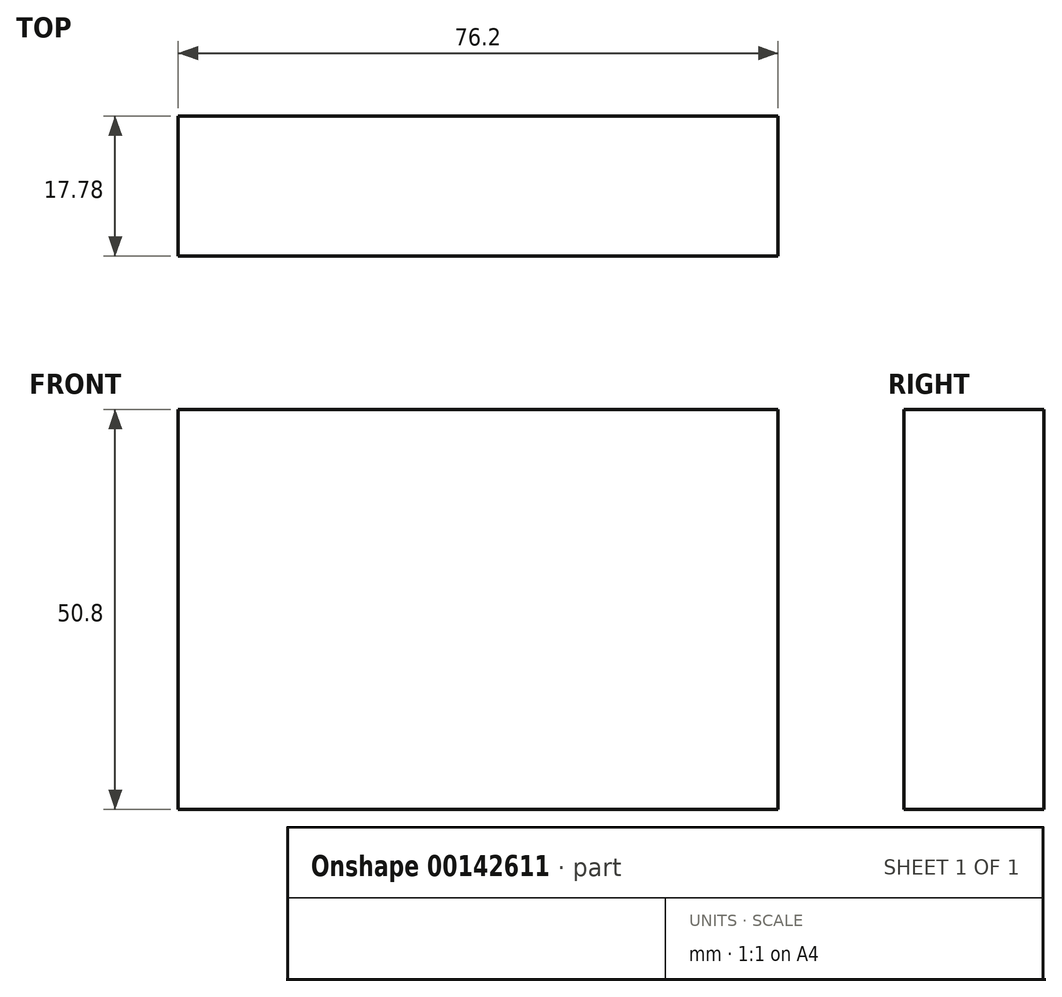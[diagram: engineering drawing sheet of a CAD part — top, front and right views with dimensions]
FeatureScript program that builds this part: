
annotation { "Feature Type Name" : "Feature", "Feature Type Description" : "" }
export const myFeature = defineFeature(function(context is Context, id is Id, definition is map)
    precondition{}
    {
        {
            var Q0;
            Q0=qCreatedBy(makeId("Top.planeOp"),FACE);
            var sketch = newSketch(context, id + "F0", { "sketchPlane" : qUnion([Q0])});
            skLineSegment(sketch, "E0.bottom", {"start": v(-41.2, 13.04) * mm, "end": v(35, 13.04) * mm});
            skLineSegment(sketch, "E0.top", {"start": v(-41.2, -4.74) * mm, "end": v(35, -4.74) * mm});
            skLineSegment(sketch, "E0.left", {"start": v(-41.2, 13.04) * mm, "end": v(-41.2, -4.74) * mm});
            skLineSegment(sketch, "E0.right", {"start": v(35, 13.04) * mm, "end": v(35, -4.74) * mm});
            skSolve(sketch);
        }
        {
            var Q0;
            Q0=makeQuery(id+"F0.imprint","IMPRINT",FACE,{"disambiguationData":[TD([[makeQuery(id+"F0.imprint","IMPRINT",EDGE,{"derivedFrom":sQuery(id+"F0.wireOp",EDGE,"E0.bottom")}),-1.0]])]});
            extrude(context, id + "F1", {"entities" : qUnion([Q0]), "depth" : 50.8 * mm});
        }
    });
